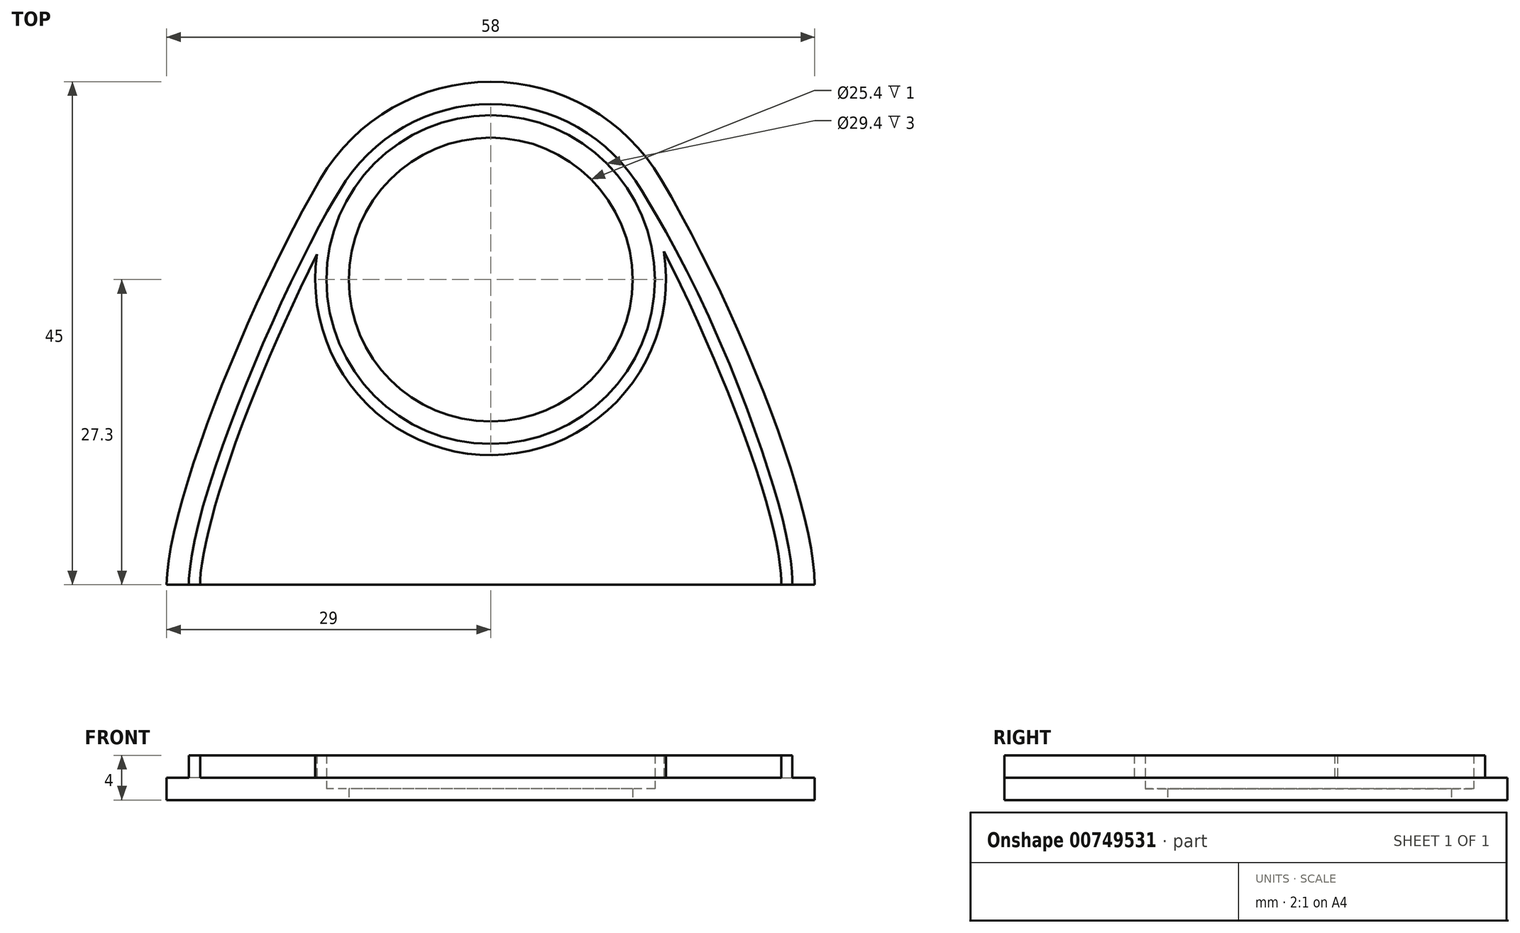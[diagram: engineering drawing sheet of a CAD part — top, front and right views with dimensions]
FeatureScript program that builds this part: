
annotation { "Feature Type Name" : "Feature", "Feature Type Description" : "" }
export const myFeature = defineFeature(function(context is Context, id is Id, definition is map)
    precondition{}
    {
        {
            var Q0;
            Q0=qCreatedBy(makeId("Top.planeOp"),FACE);
            var sketch = newSketch(context, id + "F0", { "sketchPlane" : qUnion([Q0])});
            skArc(sketch, "E0", {"start": v(15.25, 66.28) * mm, "mid": v(0, 75) * mm, "end": v(-15.25, 66.28) * mm});
            skCircle(sketch, "E1", {"center": v(0, 57.3) * mm, "radius": 12.7 * mm});
            skFitSpline(sketch, "E2", {"points": [v(-15.25, 66.28) * mm, v(-29, 30) * mm], "startDerivative": vector(-17.92, -30.43) * mm, "endDerivative": vector(0, -21.56) * mm});
            skFitSpline(sketch, "E3", {"points": [v(15.25, 66.28) * mm, v(29, 30) * mm], "startDerivative": vector(21.03, -35.71) * mm, "endDerivative": vector(0, -21.56) * mm});
            skLineSegment(sketch, "E4", {"start": v(-27, 30) * mm, "end": v(-29, 30) * mm});
            skLineSegment(sketch, "E5", {"start": v(27, 30) * mm, "end": v(29, 30) * mm});
            skLineSegment(sketch, "E6", {"start": v(-29, 30) * mm, "end": v(29, 30) * mm});
            skSolve(sketch);
        }
        {
            var Q0;
            Q0=makeQuery(id+"F0.imprint","IMPRINT",FACE,{"disambiguationData":[TD([[makeQuery(id+"F0.imprint","IMPRINT",EDGE,{"derivedFrom":sQuery(id+"F0.wireOp",EDGE,"E0")}),1.0]])]});
            extrude(context, id + "F1", {"entities" : qUnion([Q0]), "depth" : 2 * mm, "offsetDistance" : 25 * mm});
        }
        {
            var Q0;
            Q0=makeQuery(id+"F1.opExtrude","CAP_FACE",FACE,{"disambiguationData":[OSD([sQuery(id+"F0.wireOp",EDGE,"rKy58ZlB-kP61-Ok1W-jxmB-2eYKyQ9vMdYR"),sQuery(id+"F0.wireOp",EDGE,"0Ro1BS0Q-2mgt-ZydI-AfPz-EH0e96b9fWh7"),sQuery(id+"F0.wireOp",EDGE,"E1"),sQuery(id+"F0.wireOp",EDGE,"87762f92-a82d-4736-8b2d-cb61234f6977.0"),sQuery(id+"F0.wireOp",EDGE,"87762f92-a82d-4736-8b2d-cb61234f6977.2"),sQuery(id+"F0.wireOp",EDGE,"87762f92-a82d-4736-8b2d-cb61234f6977.3"),sQuery(id+"F0.wireOp",EDGE,"87762f92-a82d-4736-8b2d-cb61234f6977.5"),sQuery(id+"F0.wireOp",EDGE,"E4"),sQuery(id+"F0.wireOp",EDGE,"E5"),sQuery(id+"F0.wireOp",EDGE,"OBthIzAU-zjxL-SYiB-24dl-3B8FTxSEXE3T"),sQuery(id+"F0.wireOp",EDGE,"hQ1LHbks-fRvT-trK1-pk5m-avV33pfGG9a5")])],"isStart":false});
            var sketch = newSketch(context, id + "F2", { "sketchPlane" : qUnion([Q0])});
            skCircle(sketch, "E7", {"center": v(0, 57.3) * mm, "radius": 15.7 * mm});
            skCircle(sketch, "E8", {"center": v(0, 57.3) * mm, "radius": 14.7 * mm});
            skFitSpline(sketch, "E9.0", {"points": [v(-13.53, 65.27) * mm, v(-14.25, 64.04) * mm, v(-15.77, 61.28) * mm, v(-18.12, 56.55) * mm, v(-20.42, 51.46) * mm, v(-22.55, 46.28) * mm, v(-24.4, 41.25) * mm, v(-25.85, 36.62) * mm, v(-26.63, 33.33) * mm, v(-26.95, 31.21) * mm, v(-27, 30.36) * mm, v(-27, 30) * mm]});
            skFitSpline(sketch, "E10.0", {"points": [v(-12.67, 64.76) * mm, v(-13.38, 63.55) * mm, v(-14.88, 60.82) * mm, v(-17.22, 56.12) * mm, v(-19.5, 51.07) * mm, v(-21.62, 45.92) * mm, v(-23.45, 40.92) * mm, v(-24.65, 37.11) * mm, v(-25.35, 34.42) * mm, v(-25.73, 32.62) * mm, v(-25.96, 31.1) * mm, v(-26, 30.31) * mm, v(-26, 30) * mm]});
            skFitSpline(sketch, "E11.0", {"points": [v(13.53, 65.27) * mm, v(15.25, 62.35) * mm, v(18.67, 55.84) * mm, v(22.37, 47.22) * mm, v(24.67, 40.8) * mm, v(25.98, 36.41) * mm, v(26.68, 33.28) * mm, v(26.96, 31.22) * mm, v(27, 30.37) * mm, v(27, 30) * mm]});
            skFitSpline(sketch, "E12.0", {"points": [v(12.67, 64.76) * mm, v(14.37, 61.88) * mm, v(16.91, 57.02) * mm, v(19.97, 50.27) * mm, v(22, 45.26) * mm, v(23.72, 40.48) * mm, v(25.02, 36.15) * mm, v(25.7, 33.1) * mm, v(25.96, 31.12) * mm, v(26, 30.33) * mm, v(26, 30) * mm]});
            skSolve(sketch);
        }
        {
            var Q0;
            Q0=makeQuery(id+"F2.imprint","IMPRINT",FACE,{"disambiguationData":[TD([[makeQuery(id+"F2.imprint","IMPRINT",EDGE,{"derivedFrom":sQuery(id+"F2.wireOp",EDGE,"E7")}),1.0]])]});
            var Q1;
            {var subQ0=sQuery(id+"F2.wireOp",EDGE,"E9.0");Q1=makeQuery(id+"F2.imprint","IMPRINT",FACE,{"disambiguationData":[TD([[makeQuery(id+"F2.imprint","IMPRINT",EDGE,{"derivedFrom":subQ0}),1.0]])]});}
            var Q2;
            {var subQ0=sQuery(id+"F2.wireOp",EDGE,"E11.0");Q2=makeQuery(id+"F2.imprint","IMPRINT",FACE,{"disambiguationData":[TD([[makeQuery(id+"F2.imprint","IMPRINT",EDGE,{"derivedFrom":subQ0}),-1.0]])]});}
            var Q3;
            {var subQ0=sQuery(id+"F2.wireOp",EDGE,"E12.0");var subQ1=sQuery(id+"F2.wireOp",EDGE,"E7");var subQ2=makeQuery(id+"F2.imprint","INTERSECT",VERTEX,{"derivedFrom":[subQ1,subQ0]});Q3=makeQuery(id+"F2.imprint","IMPRINT",FACE,{"disambiguationData":[TD([[makeQuery(id+"F2.imprint","IMPRINT",EDGE,{"disambiguationData":[TD([[subQ2,1.0]])],"derivedFrom":subQ1}),1.0]])]});}
            extrude(context, id + "F3", {"entities" : qUnion([Q0, Q1, Q2, Q3]), "operationType" : NewBodyOperationType.ADD, "depth" : 2 * mm, "offsetDistance" : 25 * mm});
        }
        {
            var Q0;
            {var subQ0=sQuery(id+"F0.wireOp",EDGE,"E1");Q0=makeQuery(id+"F3.boolean.opBoolean","SPLIT",FACE,{"disambiguationData":[TD([makeQuery(id+"F1.opExtrude","SWEPT_FACE",FACE,{"disambiguationData":[OSD([subQ0])]})])],"derivedFrom":makeQuery(id+"F1.opExtrude","CAP_FACE",FACE,{"disambiguationData":[OSD([sQuery(id+"F0.wireOp",EDGE,"E0"),subQ0,sQuery(id+"F0.wireOp",EDGE,"E2"),sQuery(id+"F0.wireOp",EDGE,"E3"),sQuery(id+"F0.wireOp",EDGE,"E6")])],"isStart":false})});}
            extrude(context, id + "F4", {"entities" : qUnion([Q0]), "operationType" : NewBodyOperationType.REMOVE, "oppositeDirection" : true, "depth" : 1 * mm, "offsetDistance" : 25 * mm});
        }
    });
